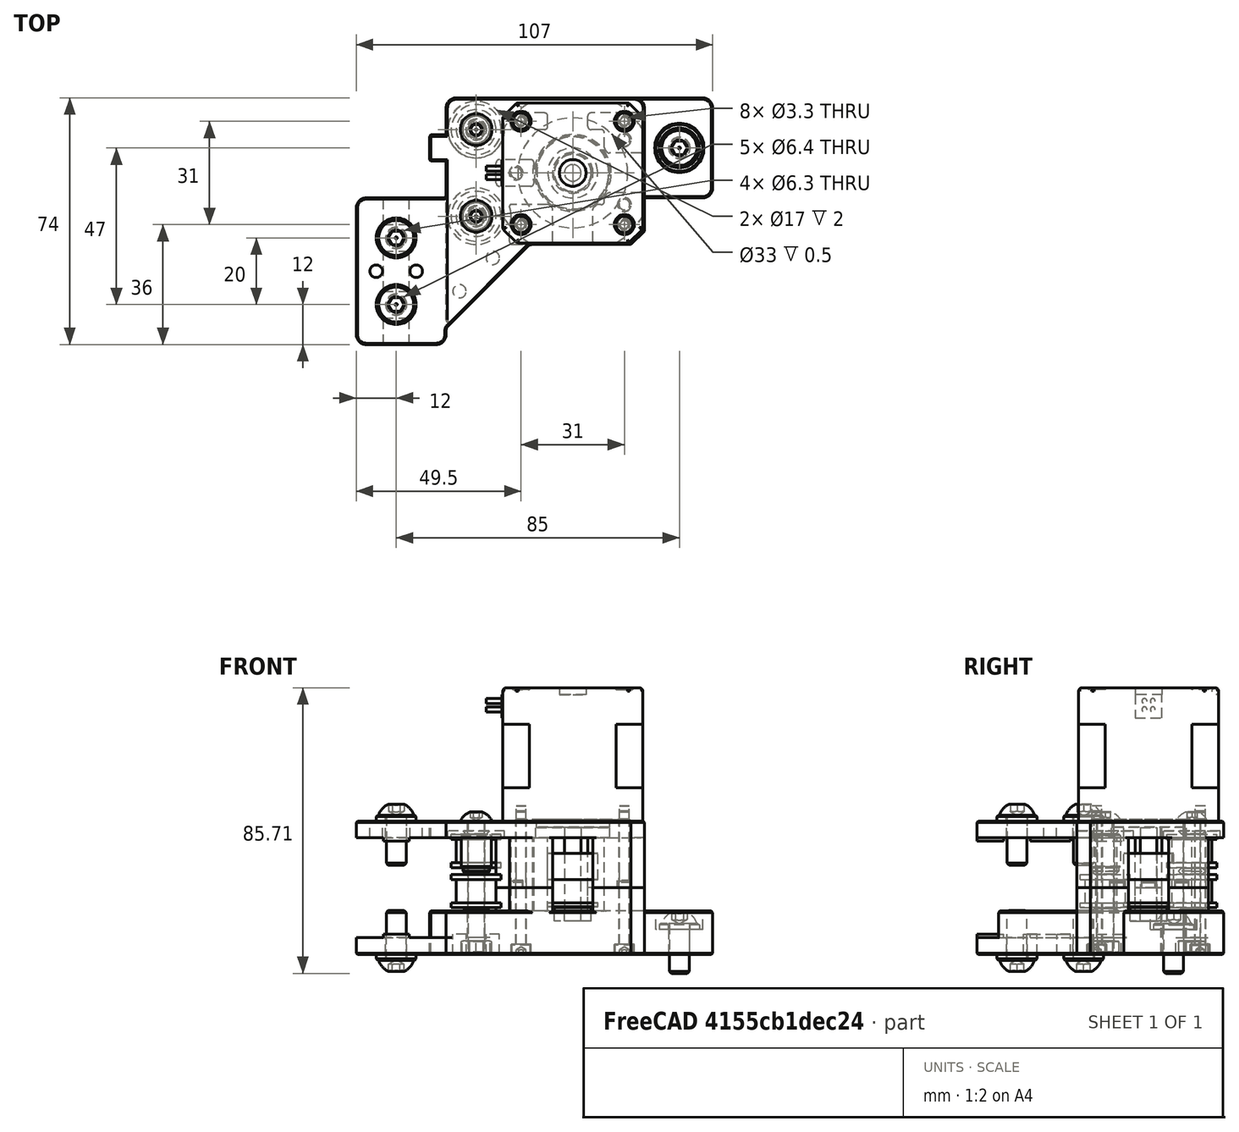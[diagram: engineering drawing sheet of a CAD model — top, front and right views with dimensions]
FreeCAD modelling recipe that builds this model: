
FCSTD DOCUMENT  (FreeCAD 0.19R24291 (Git))
Label: left-motor-assembly
License: Other
LicenseURL: GPL3
objects: Part::FeaturePython×18, Part::Feature×10, App::DocumentObjectGroup×2, PartDesign::CoordinateSystem×1, App::FeaturePython×1, App::Link×1, App::Part×1
note: 29 computed .brp shape members not serialized (recipe doc carries the construction recipe); baked Part::Feature solids carry a one-line shape summary decoded from their .brp
EXTERNAL_REF file=panel-mount-assembly.FCStd obj=Part

FEATURE [Part::Feature] Cut002007  label="smooth-idler-6mm006"
  Placement = pos=(9,-35.5,9) rot=(0,0,-1;1.5708rad)
  shape: bbox 15 x 15 x 10 mm, 8 faces (baked)
FEATURE [Part::Feature] Cut002005  label="smooth-idler-6mm004"
  Placement = pos=(9,-9.5,9) rot=(0,0,-1;1.5708rad)
  shape: bbox 15 x 15 x 10 mm, 8 faces (baked)
FEATURE [Part::Feature] Cut001  label="smooth-idler-6mm"
  Placement = pos=(9,-9.5,21) rot=(0,0,-1;1.5708rad)
  shape: bbox 15 x 15 x 10 mm, 8 faces (baked)
FEATURE [Part::Feature] Cut002008017  label="dummy-idler"
  Placement = pos=(9,-35.5,31) rot=(0,1,0;3.14159rad)
  shape: bbox 9 x 9 x 11.85 mm, 9 faces (baked)
FEATURE [Part::Feature] Cut002001  label="20t-pulley001"
  Placement = pos=(38,-22.5,9.3) rot=(0,0,1;0rad)
  shape: bbox 15 x 15 x 16 mm, 8 faces (baked)
FEATURE [Part::Feature] Fusion006002011004053036004001001  label="motor-40mm"
  Placement = pos=(38,-22.5,75) rot=(0.707107,0.707107,0;3.14159rad)
  shape: bbox 47 x 42 x 67 mm, 100 faces (baked)
FEATURE [Part::Feature] Cut002008018  label="MR115ZZ"
  Placement = pos=(38,-22.5,5) rot=(0,0,1;0rad)
  shape: bbox 11 x 11 x 4 mm, 4 faces (baked)
FEATURE [Part::Feature] Cut002008019  label="spacer"
  Placement = pos=(9,-9.5,20) rot=(0,0,1;0rad)
  shape: bbox 8 x 8 x 1.7 mm, 5 faces (baked)
FEATURE [Part::FeaturePython] Washer  label="M6-Washer"  # Fasteners workbench fastener (typed FeaturePython)
  Placement = pos=(-15,-42,35) rot=(0,0,1;0rad)
  diameter = 2
  invert = false
  matchOuter = true
  offset = 0
  type = 4
FEATURE [Part::FeaturePython] Washer001  label="M6-Washer007"  # Fasteners workbench fastener (typed FeaturePython)
  Placement = pos=(-15,-62,35) rot=(0,0,1;0rad)
  diameter = 2
  invert = false
  matchOuter = true
  offset = 0
  type = 4
FEATURE [Part::FeaturePython] Washer002  label="M6-Washer008"  # Fasteners workbench fastener (typed FeaturePython)
  Placement = pos=(-15,-42,-5) rot=(1,0,0;3.14159rad)
  diameter = 2
  invert = true
  matchOuter = true
  offset = 0
  type = 4
FEATURE [Part::FeaturePython] Washer003  label="M6-Washer009"  # Fasteners workbench fastener (typed FeaturePython)
  Placement = pos=(-15,-62,-5) rot=(1,0,0;3.14159rad)
  diameter = 2
  invert = true
  matchOuter = true
  offset = 0
  type = 4
FEATURE [Part::FeaturePython] Washer004  label="M6-Washer010"  # Fasteners workbench fastener (typed FeaturePython)
  Placement = pos=(70,-15,2.5) rot=(0,0,1;0rad)
  diameter = 2
  invert = false
  matchOuter = true
  offset = 0
  type = 4
FEATURE [Part::FeaturePython] Nut  label="M5-Nut"  # Fasteners workbench fastener (typed FeaturePython)
  Placement = pos=(9,-9.5,-1) rot=(1,0,0;3.14159rad)
  diameter = 7
  invert = true
  matchOuter = true
  offset = 0
  thread = false
  type = 7
FEATURE [Part::FeaturePython] Nut001  label="M5-Nut001"  # Fasteners workbench fastener (typed FeaturePython)
  Placement = pos=(9,-35.5,-1) rot=(1,0,0;3.14159rad)
  diameter = 7
  invert = true
  matchOuter = true
  offset = 0
  thread = false
  type = 7
FEATURE [Part::FeaturePython] Screw  label="M3x40-Screw"  # Fasteners workbench fastener (typed FeaturePython)
  Placement = pos=(53.5,-7,-2) rot=(1,0,0;3.14159rad)
  diameter = 4
  invert = true
  length = 10
  lengthCustom = 40
  matchOuter = true
  offset = 0
  thread = false
  type = 33
FEATURE [Part::FeaturePython] Screw001  label="M3x40-Screw007"  # Fasteners workbench fastener (typed FeaturePython)
  Placement = pos=(22.5,-7,-2) rot=(1,0,0;3.14159rad)
  diameter = 4
  invert = true
  length = 10
  lengthCustom = 40
  matchOuter = true
  offset = 0
  thread = false
  type = 33
FEATURE [Part::FeaturePython] Screw002  label="M3x40-Screw008"  # Fasteners workbench fastener (typed FeaturePython)
  Placement = pos=(22.5,-38,-2) rot=(1,0,0;3.14159rad)
  diameter = 4
  invert = true
  length = 10
  lengthCustom = 40
  matchOuter = true
  offset = 0
  thread = false
  type = 33
FEATURE [Part::FeaturePython] Screw003  label="M3x40-Screw006"  # Fasteners workbench fastener (typed FeaturePython)
  Placement = pos=(53.5,-38,-2) rot=(1,0,0;3.14159rad)
  diameter = 4
  invert = true
  length = 10
  lengthCustom = 40
  matchOuter = true
  offset = 0
  thread = false
  type = 33
FEATURE [Part::FeaturePython] Screw004  label="M6x15-Screw004"  # Fasteners workbench fastener (typed FeaturePython)
  Placement = pos=(70,-15,4.3) rot=(0,0,1;0rad)
  baseObject = -> Washer004 [Edge1]
  diameter = 4
  invert = false
  length = 13
  lengthCustom = 15
  matchOuter = true
  offset = 0
  thread = false
  type = 39
FEATURE [Part::FeaturePython] Screw005  label="M6x15-Screw001"  # Fasteners workbench fastener (typed FeaturePython)
  Placement = pos=(-15,-42,36.8) rot=(0,0,1;0rad)
  baseObject = -> Washer [Edge1]
  diameter = 4
  invert = false
  length = 13
  lengthCustom = 15
  matchOuter = true
  offset = 0
  thread = false
  type = 39
FEATURE [Part::FeaturePython] Screw006  label="M6x15-Screw"  # Fasteners workbench fastener (typed FeaturePython)
  Placement = pos=(-15,-62,36.8) rot=(0,0,1;0rad)
  baseObject = -> Washer001 [Edge1]
  diameter = 4
  invert = false
  length = 13
  lengthCustom = 15
  matchOuter = true
  offset = 0
  thread = false
  type = 39
FEATURE [Part::FeaturePython] Screw007  label="M6x15-Screw003"  # Fasteners workbench fastener (typed FeaturePython)
  Placement = pos=(-15,-62,-6.8) rot=(1,0,0;3.14159rad)
  baseObject = -> Washer003 [Edge1]
  diameter = 4
  invert = false
  length = 13
  lengthCustom = 15
  matchOuter = true
  offset = 0
  thread = false
  type = 39
FEATURE [Part::FeaturePython] Screw008  label="M6x15-Screw002"  # Fasteners workbench fastener (typed FeaturePython)
  Placement = pos=(-15,-42,-6.8) rot=(1,0,0;3.14159rad)
  baseObject = -> Washer002 [Edge1]
  diameter = 4
  invert = false
  length = 13
  lengthCustom = 15
  matchOuter = true
  offset = 0
  thread = false
  type = 39
FEATURE [Part::FeaturePython] Screw009  label="M5x40-Screw"  # Fasteners workbench fastener (typed FeaturePython)
  Placement = pos=(9,-35.5,35) rot=(0,0,1;0rad)
  diameter = 3
  invert = false
  length = 12
  lengthCustom = 40
  matchOuter = true
  offset = 0
  thread = false
  type = 39
FEATURE [Part::FeaturePython] Screw010  label="M5x40-Screw001"  # Fasteners workbench fastener (typed FeaturePython)
  Placement = pos=(9,-9.5,35) rot=(0,0,1;0rad)
  diameter = 3
  invert = false
  length = 12
  lengthCustom = 40
  matchOuter = true
  offset = 0
  thread = false
  type = 39
FEATURE [Part::Feature] Chamfer041001
  Placement = pos=(0,-30,0) rot=(0,0,1;0rad)
  shape: bbox 86.5 x 74 x 20 mm, 149 faces (baked)
FEATURE [Part::Feature] Chamfer042001
  Placement = pos=(0,-30,0) rot=(0,0,1;0rad)
  shape: bbox 107 x 74 x 22 mm, 215 faces (baked)
FEATURE [App::DocumentObjectGroup] Parts
  Group = -> [Washer,Washer001,Washer002,Washer003,Washer004]
FEATURE [PartDesign::CoordinateSystem] LCS_Origin
  AttacherType = Attacher::AttachEngine3D
  MapMode = 2
  Support = -> [X_Axis001]
FEATURE [App::DocumentObjectGroup] Constraints
FEATURE [App::FeaturePython] Variables  # WARN: FeaturePython — macro-defined, semantics opaque (R4)
FEATURE [App::Link] panel_mount_assembly_Panel_mounterr2_000  label="panel_mount_assembly_Panel-mounterr2-000"
  LinkedObject = -> <external panel-mount-assembly.FCStd>#Part
FEATURE [App::Part] Model
  Configuration = 0
  Group = -> [LCS_Origin,Constraints,Variables,Chamfer042001,Chamfer041001,Screw010,Cut002008018,Cut002001,Fusion006002011004053036004001001,Washer002,Screw008,Washer003,Screw007,Washer001,Screw006,Washer,Screw005,Washer004,Screw004,Cut002008017,Cut001,Cut002007,Cut002005,Screw002,Screw001,Screw,Nut001,Nut,panel_mount_assembly_Panel_mounterr2_000]
  Origin = -> Origin001
  Type = Assembly4 Model

RESOLVED EXTERNAL PARTS (link-assembly join: the EXTERNAL_REF files above that resolve inside this repo's crawl, each included once):
---- part panel-mount-assembly.FCStd = doc fcstd_32d5bfa225ab ----
FCSTD DOCUMENT  (FreeCAD 0.19R24291 (Git))
Label: panel-mount-assembly
License: Other
LicenseURL: GPL3
objects: Part::Feature×2, Part::FeaturePython×1, PartDesign::Point×1, Part::Box×1, App::Part×1
note: 5 computed .brp shape members not serialized (recipe doc carries the construction recipe); baked Part::Feature solids carry a one-line shape summary decoded from their .brp

FEATURE [Part::Feature] Chamfer008001001
  shape: bbox 28 x 22 x 6 mm, 82 faces (baked)
FEATURE [Part::Feature] Chamfer008002001001
  shape: bbox 17 x 28 x 11 mm, 53 faces (baked)
FEATURE [Part::FeaturePython] Screw  label="M6x16-Screw"  # Fasteners workbench fastener (typed FeaturePython)
  Placement = pos=(15,0,7) rot=(0,0,1;0rad)
  baseObject = -> Chamfer008002001001 [Edge135]
  diameter = 4
  invert = false
  length = 3
  lengthCustom = 16
  matchOuter = false
  offset = 0
  thread = false
  type = 40
FEATURE [PartDesign::Point] Point_Panel_mounterr2_000_1  label="Point_Panel-mounterr2-000_1"
  AttacherType = Attacher::AttachEnginePoint
  AttachmentOffset = pos=(0,5,0) rot=(0,0,1;0rad)
  MapMode = 36
  Placement = pos=(15,1.1e-15,-4) rot=(1,0,0;1.5708rad)
  Support = -> [Screw]
FEATURE [Part::Box] Box  label="Cube"
  AttacherType = Attacher::AttachEngine3D
  Height = 10
  Length = 10
  Width = 10
FEATURE [App::Part] Part  label="Panel-mounterr2-000"
  Group = -> [Chamfer008001001,Chamfer008002001001,Screw,Point_Panel_mounterr2_000_1,Box]
  Origin = -> Origin
